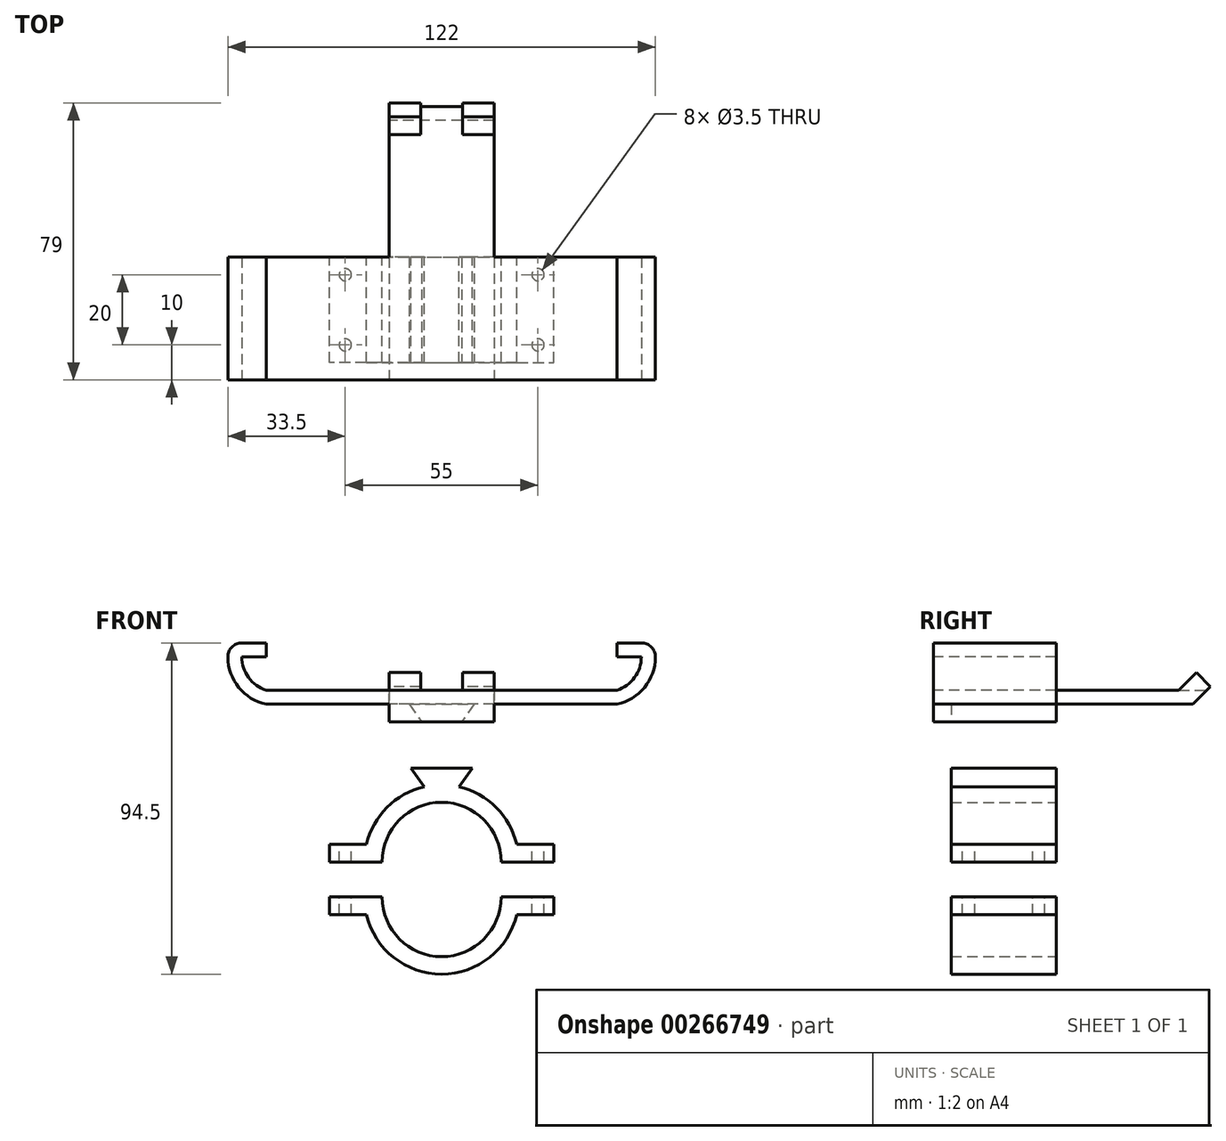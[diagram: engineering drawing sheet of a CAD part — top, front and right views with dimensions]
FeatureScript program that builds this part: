
annotation { "Feature Type Name" : "Feature", "Feature Type Description" : "" }
export const myFeature = defineFeature(function(context is Context, id is Id, definition is map)
    precondition{}
    {
        {
            var Q0;
            Q0=qCreatedBy(makeId("Front.planeOp"),FACE);
            var sketch = newSketch(context, id + "F0", { "sketchPlane" : qUnion([Q0])});
            skArc(sketch, "E0", {"start": v(17, 0) * mm, "mid": v(0, 17) * mm, "end": v(-17, 0) * mm});
            skArc(sketch, "E1", {"start": v(22, 0) * mm, "mid": v(0, 22) * mm, "end": v(-22, 0) * mm});
            skLineSegment(sketch, "E2", {"start": v(17, 0) * mm, "end": v(-17, 0) * mm, "construction": true});
            skLineSegment(sketch, "E3", {"start": v(22, 0) * mm, "end": v(17, 0) * mm});
            skLineSegment(sketch, "E4", {"start": v(-17, 0) * mm, "end": v(-22, 0) * mm});
            skLineSegment(sketch, "E5.bottom", {"start": v(17, 0) * mm, "end": v(32, 0) * mm});
            skLineSegment(sketch, "E5.top", {"start": v(17, 5) * mm, "end": v(32, 5) * mm});
            skLineSegment(sketch, "E5.left", {"start": v(17, 0) * mm, "end": v(17, 5) * mm});
            skLineSegment(sketch, "E5.right", {"start": v(32, 0) * mm, "end": v(32, 5) * mm});
            skLineSegment(sketch, "E6.bottom", {"start": v(-17, 0) * mm, "end": v(-32, 0) * mm});
            skLineSegment(sketch, "E6.top", {"start": v(-17, 5) * mm, "end": v(-32, 5) * mm});
            skLineSegment(sketch, "E6.left", {"start": v(-17, 0) * mm, "end": v(-17, 5) * mm});
            skLineSegment(sketch, "E6.right", {"start": v(-32, 0) * mm, "end": v(-32, 5) * mm});
            skLineSegment(sketch, "E7", {"start": v(-17, -10) * mm, "end": v(17, -10) * mm, "construction": true});
            skArc(sketch, "E8", {"start": v(-17, -10) * mm, "mid": v(0, -27) * mm, "end": v(17, -10) * mm});
            skLineSegment(sketch, "E9", {"start": v(17, -10) * mm, "end": v(22, -10) * mm});
            skLineSegment(sketch, "E10", {"start": v(-17, -10) * mm, "end": v(-22, -10) * mm});
            skArc(sketch, "E11", {"start": v(-22, -10) * mm, "mid": v(0, -32) * mm, "end": v(22, -10) * mm});
            skLineSegment(sketch, "E12.bottom", {"start": v(17, -10) * mm, "end": v(32, -10) * mm});
            skLineSegment(sketch, "E12.top", {"start": v(17, -15) * mm, "end": v(32, -15) * mm});
            skLineSegment(sketch, "E12.left", {"start": v(17, -10) * mm, "end": v(17, -15) * mm});
            skLineSegment(sketch, "E12.right", {"start": v(32, -10) * mm, "end": v(32, -15) * mm});
            skPoint(sketch, "E13.oppositeSnap0", {"position": v(24.5, -15) * mm});
            skLineSegment(sketch, "E13.bottom", {"start": v(-17, -10) * mm, "end": v(-32, -10) * mm});
            skLineSegment(sketch, "E13.top", {"start": v(-17, -15) * mm, "end": v(-32, -15) * mm});
            skLineSegment(sketch, "E13.left", {"start": v(-17, -10) * mm, "end": v(-17, -15) * mm});
            skLineSegment(sketch, "E13.right", {"start": v(-32, -10) * mm, "end": v(-32, -15) * mm});
            skPoint(sketch, "E14", {"position": v(0, 21.42) * mm});
            skLineSegment(sketch, "E15", {"start": v(-5, 21.42) * mm, "end": v(5, 21.42) * mm, "construction": true});
            skLineSegment(sketch, "E16", {"start": v(-5, 21.42) * mm, "end": v(-8.75, 26.78) * mm});
            skLineSegment(sketch, "E17", {"start": v(-8.75, 26.78) * mm, "end": v(8.75, 26.78) * mm});
            skLineSegment(sketch, "E18", {"start": v(8.75, 26.78) * mm, "end": v(5, 21.42) * mm});
            skPoint(sketch, "E19.endSnap0", {"position": v(0, 17) * mm});
            skSolve(sketch);
        }
        {
            var Q0;
            Q0=qCreatedBy(makeId("Front.planeOp"),FACE);
            cPlane(context, id + "F1", {"entities" : qUnion([Q0]), "cplaneType" : CPlaneType.OFFSET, "offset" : 30 * mm, "width" : 150 * mm, "height" : 150 * mm});
        }
        {
            var Q0;
            Q0=qCreatedBy(id+"F1.planeOp",FACE);
            var sketch = newSketch(context, id + "F2", { "sketchPlane" : qUnion([Q0])});
            skLineSegment(sketch, "E20", {"start": v(-50, 49) * mm, "end": v(50, 49) * mm});
            skLineSegment(sketch, "E21", {"start": v(-57, 58.5) * mm, "end": v(57, 58.5) * mm, "construction": true});
            skLineSegment(sketch, "E22", {"start": v(0, 49) * mm, "end": v(0, 58.5) * mm, "construction": true});
            skArc(sketch, "E23", {"start": v(50, 49) * mm, "mid": v(55.06, 52.6) * mm, "end": v(57, 58.5) * mm});
            skArc(sketch, "E24", {"start": v(-57, 58.5) * mm, "mid": v(-55.06, 52.6) * mm, "end": v(-50, 49) * mm});
            skLineSegment(sketch, "E25", {"start": v(-9.25, 45) * mm, "end": v(9.25, 45) * mm});
            skLineSegment(sketch, "E26", {"start": v(9.25, 45) * mm, "end": v(5.75, 40) * mm});
            skLineSegment(sketch, "E27", {"start": v(-9.25, 45) * mm, "end": v(-5.75, 40) * mm});
            skLineSegment(sketch, "E28", {"start": v(57, 58.5) * mm, "end": v(50, 58.5) * mm});
            skLineSegment(sketch, "E29", {"start": v(50, 58.5) * mm, "end": v(50, 62.5) * mm});
            skLineSegment(sketch, "E30", {"start": v(50, 62.5) * mm, "end": v(57, 62.5) * mm});
            skLineSegment(sketch, "E31", {"start": v(5.75, 40) * mm, "end": v(15, 40) * mm});
            skLineSegment(sketch, "E32", {"start": v(15, 40) * mm, "end": v(15, 45) * mm});
            skLineSegment(sketch, "E33", {"start": v(15, 45) * mm, "end": v(50, 45) * mm});
            skArc(sketch, "E34", {"start": v(50, 45) * mm, "mid": v(57.9, 49.8) * mm, "end": v(61, 58.5) * mm});
            skLineSegment(sketch, "E35", {"start": v(-5.75, 40) * mm, "end": v(-15, 40) * mm});
            skLineSegment(sketch, "E36", {"start": v(-15, 40) * mm, "end": v(-15, 45) * mm});
            skLineSegment(sketch, "E37", {"start": v(-15, 45) * mm, "end": v(-50, 45) * mm});
            skLineSegment(sketch, "E38", {"start": v(-57, 58.5) * mm, "end": v(-50, 58.5) * mm});
            skLineSegment(sketch, "E39", {"start": v(-50, 58.5) * mm, "end": v(-50, 62.5) * mm});
            skLineSegment(sketch, "E40", {"start": v(-50, 62.5) * mm, "end": v(-57, 62.5) * mm});
            skArc(sketch, "E41", {"start": v(-61, 58.5) * mm, "mid": v(-57.9, 49.8) * mm, "end": v(-50, 45) * mm});
            skArc(sketch, "E42", {"start": v(61, 58.5) * mm, "mid": v(59.83, 61.33) * mm, "end": v(57, 62.5) * mm});
            skArc(sketch, "E43", {"start": v(-57, 62.5) * mm, "mid": v(-59.83, 61.33) * mm, "end": v(-61, 58.5) * mm});
            skPoint(sketch, "E44", {"position": v(0, 45) * mm});
            skLineSegment(sketch, "E45", {"start": v(-5.75, 40) * mm, "end": v(5.75, 40) * mm});
            skLineSegment(sketch, "E46", {"start": v(0, 40) * mm, "end": v(0, 0) * mm, "construction": true});
            skSolve(sketch);
        }
        {
            var Q0;
            Q0=makeQuery(id+"F0.imprint","IMPRINT",FACE,{"disambiguationData":[TD([[makeQuery(id+"F0.imprint","IMPRINT",EDGE,{"derivedFrom":sQuery(id+"F0.wireOp",EDGE,"mbzJrH7V-MKxJ-bzjF-v4ra-i13s79XAPloW")}),-1.0]])]});
            var Q1;
            Q1=makeQuery(id+"F2.imprint","IMPRINT",FACE,{"disambiguationData":[TD([[makeQuery(id+"F2.imprint","IMPRINT",EDGE,{"derivedFrom":sQuery(id+"F2.wireOp",EDGE,"E20")}),-1.0]])]});
            extrude(context, id + "F3", {"entities" : qUnion([Q0, Q1]), "oppositeDirection" : true, "depth" : 30 * mm});
        }
        {
            var Q0;
            Q0=makeQuery(id+"F2.imprint","IMPRINT",FACE,{"disambiguationData":[TD([[makeQuery(id+"F2.imprint","IMPRINT",EDGE,{"derivedFrom":sQuery(id+"F2.wireOp",EDGE,"E20")}),-1.0]])]});
            var Q1;
            Q1=makeQuery(id+"F2.imprint","IMPRINT",FACE,{"disambiguationData":[TD([[makeQuery(id+"F2.imprint","IMPRINT",EDGE,{"derivedFrom":sQuery(id+"F2.wireOp",EDGE,"E25")}),-1.0]])]});
            extrude(context, id + "F4", {"entities" : qUnion([Q0, Q1]), "operationType" : NewBodyOperationType.ADD, "depth" : 5 * mm});
        }
        {
            var Q0;
            Q0=qCreatedBy(makeId("Right.planeOp"),FACE);
            var sketch = newSketch(context, id + "F5", { "sketchPlane" : qUnion([Q0])});
            skLineSegment(sketch, "E47.left", {"start": v(0, 49) * mm, "end": v(0, 45) * mm});
            skLineSegment(sketch, "E48", {"start": v(0, 49) * mm, "end": v(35, 49) * mm});
            skPoint(sketch, "E49", {"position": v(0, 58.5) * mm});
            skPoint(sketch, "E50", {"position": v(0, 62.5) * mm});
            skLineSegment(sketch, "E51", {"start": v(35, 49) * mm, "end": v(40, 54) * mm});
            skLineSegment(sketch, "E52", {"start": v(35, 49) * mm, "end": v(39, 45) * mm, "construction": true});
            skLineSegment(sketch, "E53", {"start": v(0, 45) * mm, "end": v(39, 45) * mm});
            skLineSegment(sketch, "E54", {"start": v(39, 45) * mm, "end": v(44, 50) * mm});
            skLineSegment(sketch, "E55", {"start": v(44, 50) * mm, "end": v(40, 54) * mm});
            skLineSegment(sketch, "E56", {"start": v(35, 49) * mm, "end": v(43, 49) * mm});
            skSolve(sketch);
        }
        {
            var Q0;
            Q0=qSketchRegion(id+"F5",true);
            extrude(context, id + "F6", {"entities" : qUnion([Q0]), "operationType" : NewBodyOperationType.ADD, "depth" : 15 * mm, "hasSecondDirection" : true, "secondDirectionOppositeDirection" : true, "secondDirectionDepth" : 15 * mm});
        }
        {
            var Q0;
            Q0=makeQuery(id+"F5.imprint","IMPRINT",FACE,{"disambiguationData":[TD([[makeQuery(id+"F5.imprint","IMPRINT",EDGE,{"derivedFrom":sQuery(id+"F5.wireOp",EDGE,"E51")}),-1.0]])]});
            extrude(context, id + "F7", {"entities" : qUnion([Q0]), "operationType" : NewBodyOperationType.REMOVE, "endBound" : BoundingType.SYMMETRIC, "oppositeDirection" : true, "depth" : 12 * mm, "hasSecondDirection" : true, "secondDirectionOppositeDirection" : true, "secondDirectionDepth" : 6 * mm});
        }
        {
            var Q0;
            {var subQ5=sQuery(id+"F0.wireOp",EDGE,"E6.right");Q0=makeQuery(id+"F0.imprint","IMPRINT",FACE,{"disambiguationData":[TD([[makeQuery(id+"F0.imprint","IMPRINT",EDGE,{"derivedFrom":subQ5}),-1.0]])]});}
            var Q1;
            {var subQ5=sQuery(id+"F0.wireOp",EDGE,"E6.left");Q1=makeQuery(id+"F0.imprint","IMPRINT",FACE,{"disambiguationData":[TD([[makeQuery(id+"F0.imprint","IMPRINT",EDGE,{"derivedFrom":subQ5}),1.0]])]});}
            var Q2;
            Q2=makeQuery(id+"F0.imprint","IMPRINT",FACE,{"disambiguationData":[TD([[makeQuery(id+"F0.imprint","IMPRINT",EDGE,{"derivedFrom":sQuery(id+"F0.wireOp",EDGE,"E0")}),-1.0]])]});
            var Q3;
            {var subQ5=sQuery(id+"F0.wireOp",EDGE,"E5.left");Q3=makeQuery(id+"F0.imprint","IMPRINT",FACE,{"disambiguationData":[TD([[makeQuery(id+"F0.imprint","IMPRINT",EDGE,{"derivedFrom":subQ5}),-1.0]])]});}
            var Q4;
            {var subQ5=sQuery(id+"F0.wireOp",EDGE,"E5.right");Q4=makeQuery(id+"F0.imprint","IMPRINT",FACE,{"disambiguationData":[TD([[makeQuery(id+"F0.imprint","IMPRINT",EDGE,{"derivedFrom":subQ5}),1.0]])]});}
            var Q5;
            {var subQ0=sQuery(id+"F0.wireOp",EDGE,"E16");Q5=makeQuery(id+"F0.imprint","IMPRINT",FACE,{"disambiguationData":[TD([[makeQuery(id+"F0.imprint","IMPRINT",EDGE,{"derivedFrom":subQ0}),-1.0]])]});}
            extrude(context, id + "F8", {"entities" : qUnion([Q0, Q1, Q2, Q3, Q4, Q5]), "depth" : 30 * mm});
        }
        {
            var Q0;
            {var subQ5=sQuery(id+"F0.wireOp",EDGE,"E13.right");Q0=makeQuery(id+"F0.imprint","IMPRINT",FACE,{"disambiguationData":[TD([[makeQuery(id+"F0.imprint","IMPRINT",EDGE,{"derivedFrom":subQ5}),1.0]])]});}
            var Q1;
            {var subQ5=sQuery(id+"F0.wireOp",EDGE,"E13.left");Q1=makeQuery(id+"F0.imprint","IMPRINT",FACE,{"disambiguationData":[TD([[makeQuery(id+"F0.imprint","IMPRINT",EDGE,{"derivedFrom":subQ5}),-1.0]])]});}
            var Q2;
            Q2=makeQuery(id+"F0.imprint","IMPRINT",FACE,{"disambiguationData":[TD([[makeQuery(id+"F0.imprint","IMPRINT",EDGE,{"derivedFrom":sQuery(id+"F0.wireOp",EDGE,"E8")}),-1.0]])]});
            var Q3;
            {var subQ5=sQuery(id+"F0.wireOp",EDGE,"E12.left");Q3=makeQuery(id+"F0.imprint","IMPRINT",FACE,{"disambiguationData":[TD([[makeQuery(id+"F0.imprint","IMPRINT",EDGE,{"derivedFrom":subQ5}),1.0]])]});}
            var Q4;
            {var subQ5=sQuery(id+"F0.wireOp",EDGE,"E12.right");Q4=makeQuery(id+"F0.imprint","IMPRINT",FACE,{"disambiguationData":[TD([[makeQuery(id+"F0.imprint","IMPRINT",EDGE,{"derivedFrom":subQ5}),-1.0]])]});}
            extrude(context, id + "F9", {"entities" : qUnion([Q0, Q1, Q2, Q3, Q4]), "depth" : 30 * mm});
        }
        {
            var Q0;
            Q0=makeQuery(id+"F8.opExtrude","SWEPT_FACE",FACE,{"disambiguationData":[OSD([sQuery(id+"F0.wireOp",EDGE,"E6.top")])]});
            var sketch = newSketch(context, id + "F10", { "sketchPlane" : qUnion([Q0])});
            skCircle(sketch, "E57", {"center": v(-27.5, -25) * mm, "radius": 1.75 * mm});
            skCircle(sketch, "E58", {"center": v(-27.5, -5) * mm, "radius": 1.75 * mm});
            skCircle(sketch, "E59", {"center": v(27.5, -5) * mm, "radius": 1.75 * mm});
            skCircle(sketch, "E60", {"center": v(27.5, -25) * mm, "radius": 1.75 * mm});
            skLineSegment(sketch, "E61", {"start": v(27.5, -15) * mm, "end": v(-27.5, -15) * mm, "construction": true});
            skLineSegment(sketch, "E62", {"start": v(-27.5, -5) * mm, "end": v(-27.5, -25) * mm, "construction": true});
            skLineSegment(sketch, "E63", {"start": v(27.5, -5) * mm, "end": v(27.5, -25) * mm, "construction": true});
            skLineSegment(sketch, "E64", {"start": v(0, 0) * mm, "end": v(0, -15) * mm, "construction": true});
            skSolve(sketch);
        }
        {
            var Q0;
            Q0=qSketchRegion(id+"F10",true);
            extrude(context, id + "F11", {"entities" : qUnion([Q0]), "operationType" : NewBodyOperationType.REMOVE, "oppositeDirection" : true, "depth" : 50 * mm});
        }
    });
